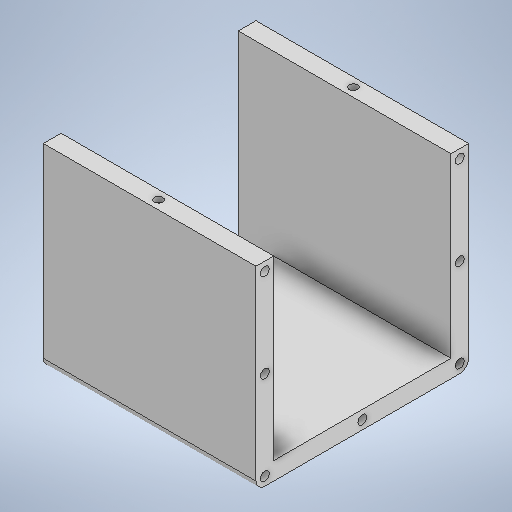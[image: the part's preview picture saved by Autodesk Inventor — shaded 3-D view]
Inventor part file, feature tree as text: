
AUTODESK INVENTOR PART (.ipt)
format: ipt  version: 2025.1 (Build 291241020, 241B)  size: 254,464 bytes
history: native  units: in
note: dims shown in document units (in); Inventor stores cm internally (conversion verified against a paired STEP export)
features: sketch x6, extrude x5, fillet x1
ambient origin geometry x8: Origin, YZ Plane, XZ Plane, XY Plane, X Axis, Y Axis, Z Axis, Center Point
bodies: Solid1 (feature_tree)
feature tree (12):
  sketch  "Sketch1"  dims[d0=6.0in d1=6.0in]
  extrude  "Extrusion1"  Depth=6.0in
  extrude  "Extrusion2"  Depth=0.5in
  fillet  "Fillet1"  Radius=0.5in
  extrude  "Extrusion3"  Depth=0.25in
  sketch  "Sketch5"  dims[d15=6.0in d16=0.2362in]
  extrude  "Extrusion5"  Depth=0.5in TaperAngle=0.0deg
  extrude  "Extrusion6"  Depth=6.0in
  sketch  "Sketch2"  dims[d2=0.5in d3=0.0in d4=0.5in d5=0.5in]
  sketch  "Sketch3"  dims[d6=5.0in d7=0.0in d8=0.25in]
  sketch  "Sketch4"  dims[d9=5.0in d11=0.5in d12=0.0in]
  sketch  "Sketch6"  dims[d17=0.2362in d18=0.1575in d19=0.0in d20=2.75in d21=0.5in d22=0.0in]
